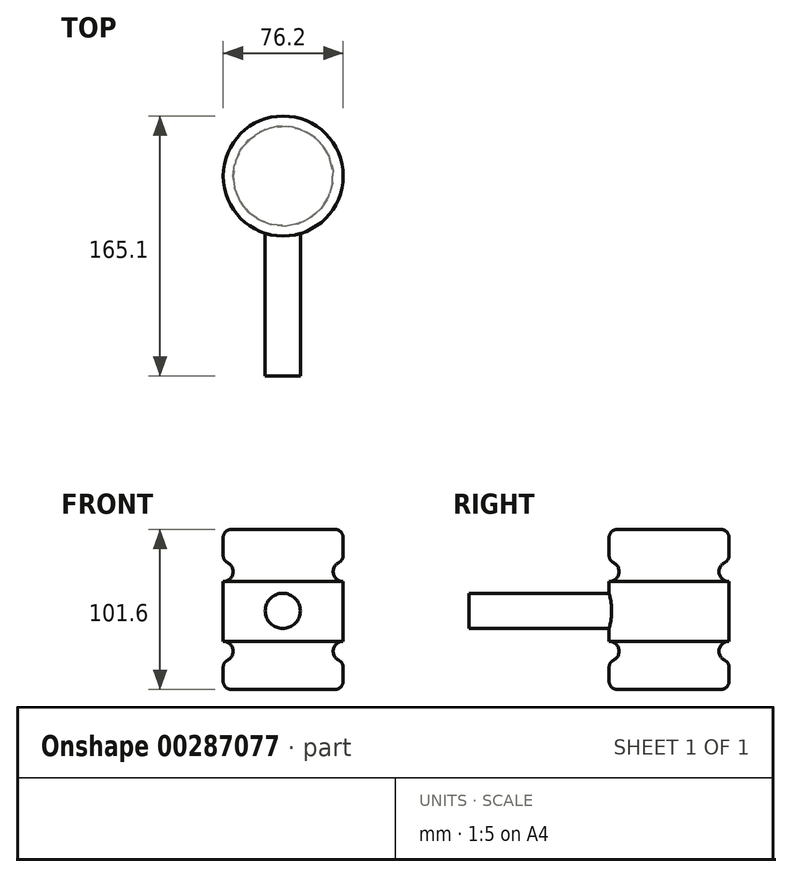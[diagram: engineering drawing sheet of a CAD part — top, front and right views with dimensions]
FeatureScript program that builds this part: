
annotation { "Feature Type Name" : "Feature", "Feature Type Description" : "" }
export const myFeature = defineFeature(function(context is Context, id is Id, definition is map)
    precondition{}
    {
        {
            var Q0;
            Q0=qCreatedBy(makeId("Front.planeOp"),FACE);
            var sketch = newSketch(context, id + "F0", { "sketchPlane" : qUnion([Q0])});
            skLineSegment(sketch, "E0.bottom", {"start": v(0, 0) * mm, "end": v(-38.1, 0) * mm});
            skLineSegment(sketch, "E0.top", {"start": v(0, 101.6) * mm, "end": v(-38.1, 101.6) * mm});
            skLineSegment(sketch, "E0.left", {"start": v(0, 0) * mm, "end": v(0, 17.93) * mm});
            skLineSegment(sketch, "E0.right", {"start": v(-38.1, 0) * mm, "end": v(-38.1, 101.6) * mm});
            skArc(sketch, "E1", {"start": v(0, 81.2) * mm, "mid": v(-6.35, 74.86) * mm, "end": v(0, 68.5) * mm});
            skArc(sketch, "E2", {"start": v(0, 30.63) * mm, "mid": v(-6.35, 24.28) * mm, "end": v(0, 17.93) * mm});
            skLineSegment(sketch, "E3.trimOffspring", {"start": v(0, 30.63) * mm, "end": v(0, 68.5) * mm});
            skLineSegment(sketch, "E4.trimOffspring", {"start": v(0, 81.2) * mm, "end": v(0, 101.6) * mm});
            skSolve(sketch);
        }
        {
            var Q0;
            Q0=makeQuery(id+"F0.imprint","IMPRINT",FACE,{"disambiguationData":[TD([[makeQuery(id+"F0.imprint","IMPRINT",EDGE,{"derivedFrom":sQuery(id+"F0.wireOp",EDGE,"E0.bottom")}),-1.0]])]});
            var Q1;
            Q1=sQuery(id+"F0.wireOp",EDGE,"E0.right");
            revolve(context, id + "F1", {"entities" : qUnion([Q0]), "axis" : qUnion([Q1]), "revolveType" : RevolveType.FULL});
        }
        {
            var Q0;
            Q0=makeQuery(id+"F1.opRevolve","SWEPT_EDGE",EDGE,{"disambiguationData":[OSD([sQuery(id+"F0.wireOp",EDGE,"E0.top"),sQuery(id+"F0.wireOp",EDGE,"E4.trimOffspring")])]});
            var Q1;
            Q1=makeQuery(id+"F1.opRevolve","SWEPT_FACE",FACE,{"disambiguationData":[OSD([sQuery(id+"F0.wireOp",EDGE,"E0.left")])]});
            var Q2;
            Q2=makeQuery(id+"F1.opRevolve","SWEPT_EDGE",EDGE,{"disambiguationData":[OSD([sQuery(id+"F0.wireOp",EDGE,"E1"),sQuery(id+"F0.wireOp",EDGE,"E4.trimOffspring")])]});
            fillet(context, id + "F2", {"entities" : qUnion([Q0, Q1, Q2]), "radius" : 5.08 * mm, "tangentPropagation" : true, "allowEdgeOverflow" : false});
        }
        {
            var Q0;
            Q0=qCreatedBy(makeId("Front.planeOp"),FACE);
            var sketch = newSketch(context, id + "F3", { "sketchPlane" : qUnion([Q0])});
            skCircle(sketch, "E5", {"center": v(-38.32, 49.9) * mm, "radius": 11.15 * mm});
            skSolve(sketch);
        }
        {
            var Q0;
            Q0 = qSketchRegion(id + "F3", true);
            extrude(context, id + "F4", {"entities" : qUnion([Q0]), "operationType" : NewBodyOperationType.ADD, "depth" : 127 * mm});
        }
    });
